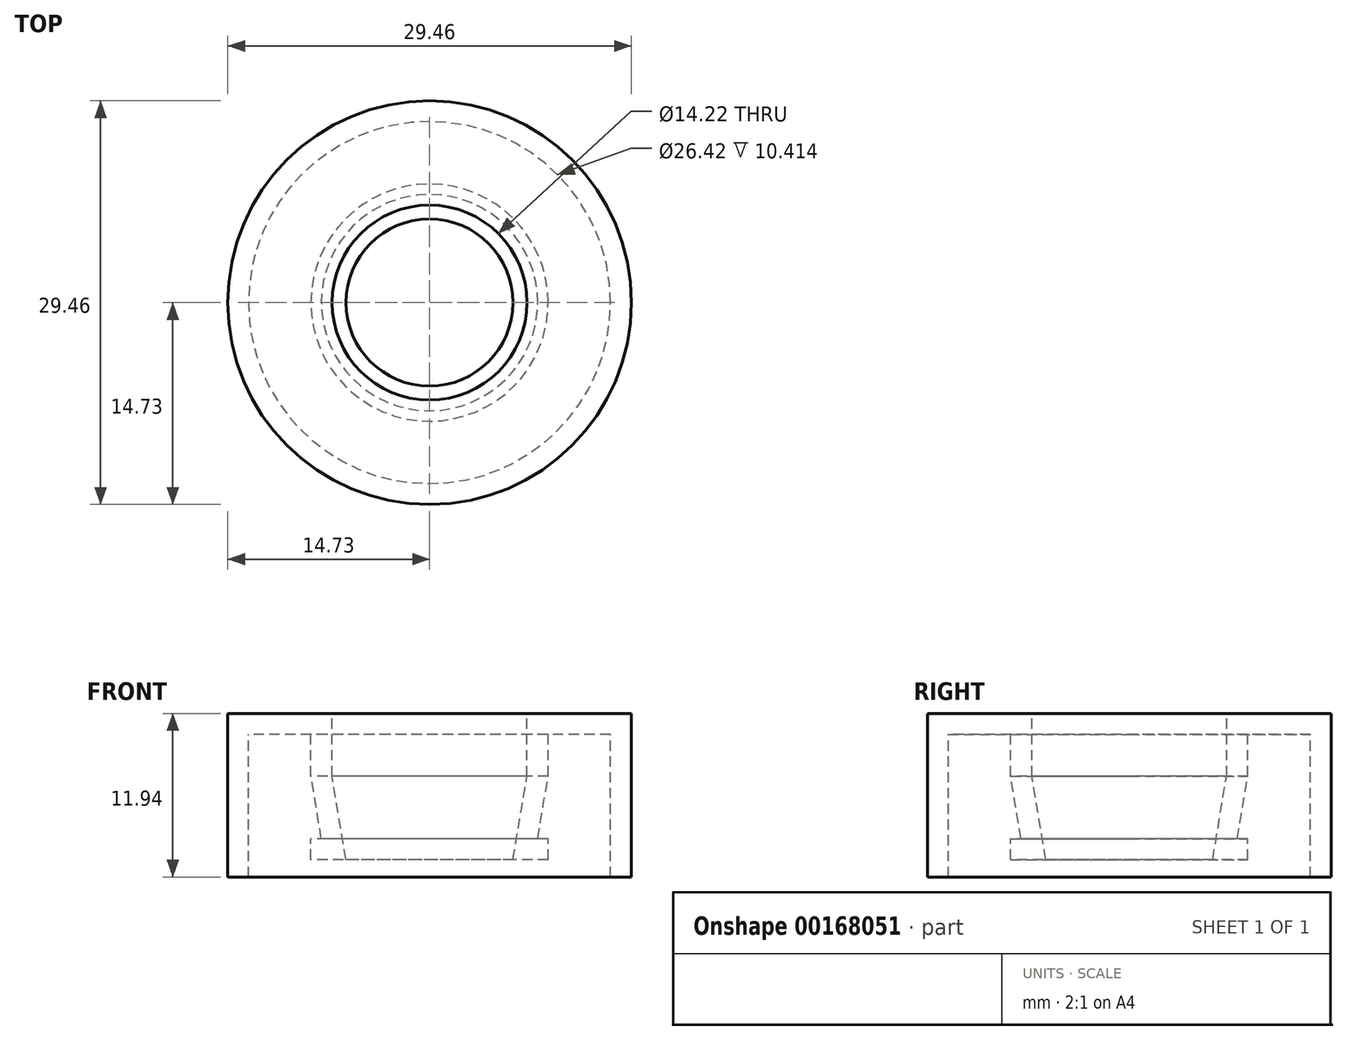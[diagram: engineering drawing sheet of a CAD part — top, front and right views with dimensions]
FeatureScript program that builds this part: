
annotation { "Feature Type Name" : "Feature", "Feature Type Description" : "" }
export const myFeature = defineFeature(function(context is Context, id is Id, definition is map)
    precondition{}
    {
        {
            var Q0;
            Q0=qCreatedBy(makeId("Front.planeOp"),FACE);
            var sketch = newSketch(context, id + "F0", { "sketchPlane" : qUnion([Q0])});
            skLineSegment(sketch, "E0", {"start": v(7.11, 0) * mm, "end": v(14.73, 0) * mm});
            skLineSegment(sketch, "E1", {"start": v(14.73, 0) * mm, "end": v(14.73, -11.94) * mm});
            skLineSegment(sketch, "E2", {"start": v(14.73, -11.94) * mm, "end": v(13.2, -11.94) * mm});
            skLineSegment(sketch, "E3", {"start": v(13.2, -11.94) * mm, "end": v(13.2, -1.52) * mm});
            skLineSegment(sketch, "E4", {"start": v(13.2, -1.52) * mm, "end": v(8.66, -1.52) * mm});
            skLineSegment(sketch, "E5", {"start": v(8.66, -1.52) * mm, "end": v(8.66, -4.57) * mm});
            skLineSegment(sketch, "E6", {"start": v(8.66, -4.57) * mm, "end": v(7.9, -9.14) * mm});
            skLineSegment(sketch, "E7", {"start": v(7.9, -9.14) * mm, "end": v(8.66, -9.14) * mm});
            skLineSegment(sketch, "E8", {"start": v(8.66, -9.14) * mm, "end": v(8.66, -10.67) * mm});
            skLineSegment(sketch, "E9", {"start": v(8.66, -10.67) * mm, "end": v(6.1, -10.67) * mm});
            skLineSegment(sketch, "E10", {"start": v(6.1, -10.67) * mm, "end": v(7.11, -4.57) * mm});
            skLineSegment(sketch, "E11", {"start": v(7.11, -4.57) * mm, "end": v(7.11, 0) * mm});
            skLineSegment(sketch, "E12", {"start": v(0, 0) * mm, "end": v(0, -16.54) * mm, "construction": true});
            skSolve(sketch);
        }
        {
            var Q0;
            Q0 = qSketchRegion(id + "F0", true);
            var Q1;
            Q1=sQuery(id+"F0.wireOp",EDGE,"E12");
            revolve(context, id + "F1", {"entities" : qUnion([Q0]), "axis" : qUnion([Q1]), "revolveType" : RevolveType.FULL});
        }
    });
